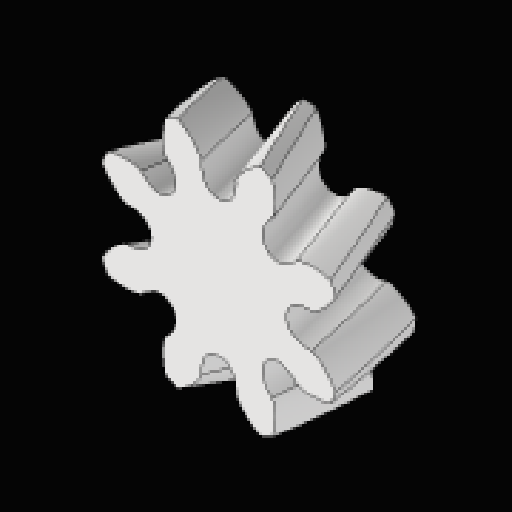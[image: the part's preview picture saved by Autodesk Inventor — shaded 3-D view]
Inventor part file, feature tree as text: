
AUTODESK INVENTOR PART (.ipt)
format: ipt  version: 2023.2 (Build 272271030, 271C)  size: 967,168 bytes
history: native  units: mm
features: sketch x3, extrude x3, projected_geometry x2, helix x1, pattern_circular x1, mirror x1
ambient origin geometry x8: Origin, YZ Plane, XZ Plane, XY Plane, X Axis, Y Axis, Z Axis, Center Point
bodies: Solid1 (feature_tree)
feature tree (11):
  sketch  "Sketch1"  dims[d0=4.5mm d1=0.0mm]
  extrude  "Extrusion1"  Depth=80.0mm TaperAngle=360.0deg
  helix  "Coil1"  [1 undecoded]
  pattern_circular  "Circular Pattern1"  [2 undecoded]
  mirror  "Mirror1"
  extrude  "Extrusion2"  [1 undecoded]
  extrude  "Extrusion3"  [1 undecoded]
  sketch  "Sketch2"  dims[d2=104.0mm d3=10.0mm d4=10.0mm d5=0.0mm d6=90.0deg d7=90.0deg d8=0.0mm d9=0.0mm d10=80.0mm d11=360.0deg d13=1.0mm d14=0.0mm]
  projected_geometry  "Projected Loop1"
  sketch  "Sketch3"  dims[d15=17.8mm d16=3.0mm d17=0.0mm]
  projected_geometry  "Projected Loop2"
note: 5 required parameter values undecoded (feature->parameter linkage not recoverable at this tier; creation-order binding heuristic only, values carry confidence <= 0.55)
